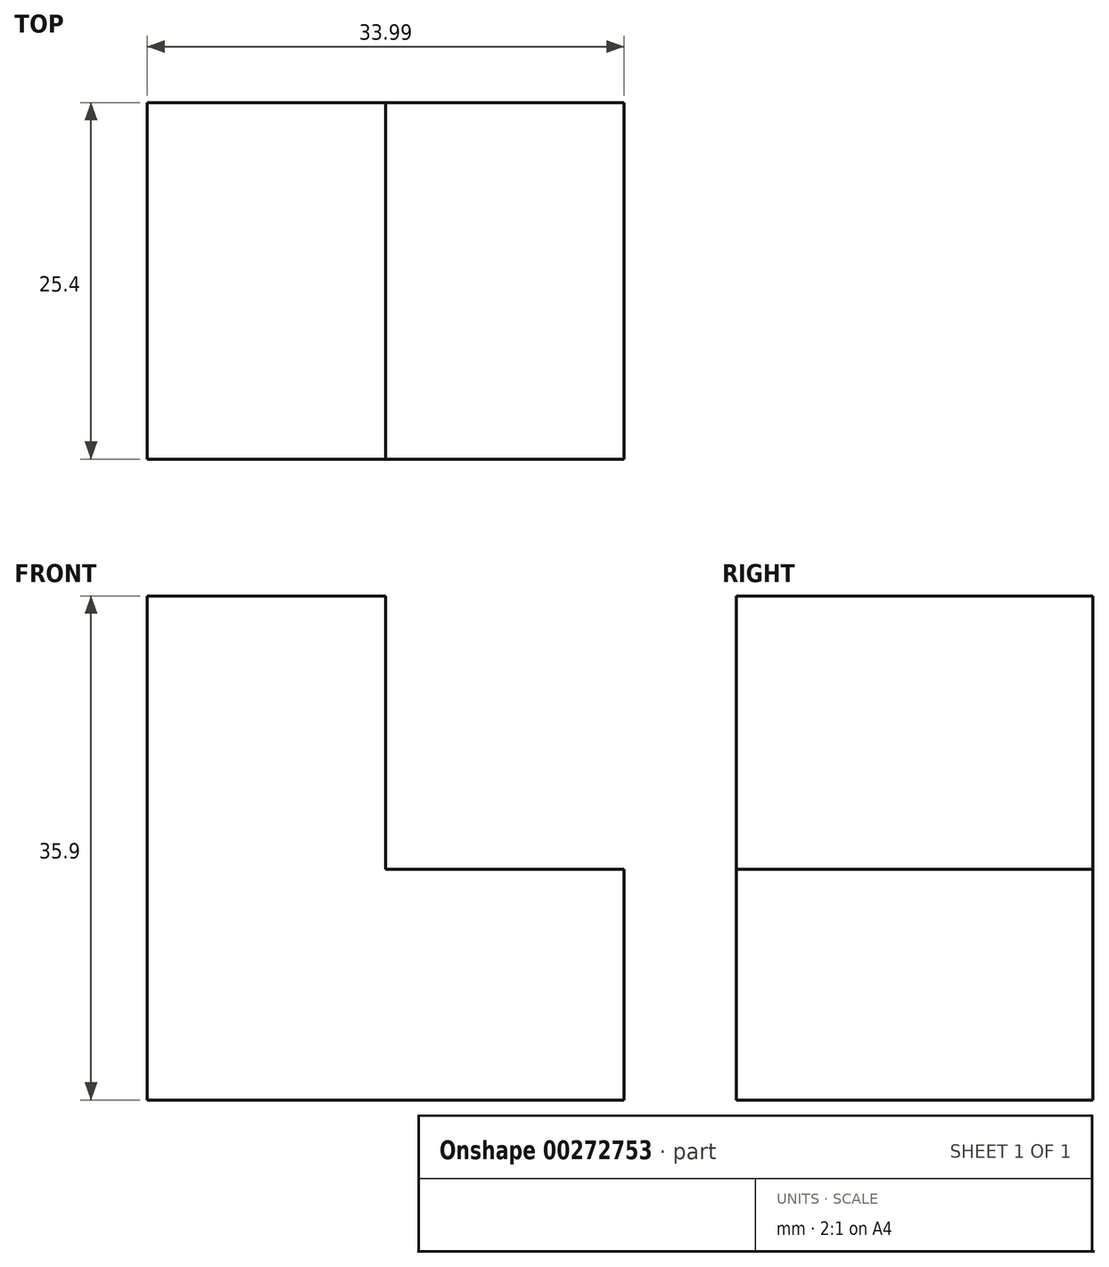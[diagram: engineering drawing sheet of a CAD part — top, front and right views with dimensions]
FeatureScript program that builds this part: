
annotation { "Feature Type Name" : "Feature", "Feature Type Description" : "" }
export const myFeature = defineFeature(function(context is Context, id is Id, definition is map)
    precondition{}
    {
        {
            var Q0;
            Q0=qCreatedBy(makeId("Front.planeOp"),FACE);
            var sketch = newSketch(context, id + "F0", { "sketchPlane" : qUnion([Q0])});
            skLineSegment(sketch, "E0", {"start": v(-60.91, 35.9) * mm, "end": v(-60.91, 0) * mm});
            skLineSegment(sketch, "E1", {"start": v(-60.91, 0) * mm, "end": v(-34.18, 0) * mm});
            skLineSegment(sketch, "E2", {"start": v(-60.91, 35.9) * mm, "end": v(-43.92, 35.9) * mm});
            skLineSegment(sketch, "E3", {"start": v(-43.92, 35.9) * mm, "end": v(-43.92, 16.42) * mm});
            skLineSegment(sketch, "E4", {"start": v(-43.92, 16.42) * mm, "end": v(-26.92, 16.42) * mm});
            skLineSegment(sketch, "E5", {"start": v(-26.92, 16.42) * mm, "end": v(-26.92, 0) * mm});
            skLineSegment(sketch, "E6", {"start": v(-26.92, 0) * mm, "end": v(-34.18, 0) * mm});
            skSolve(sketch);
        }
        {
            var Q0;
            Q0=makeQuery(id+"F0.imprint","IMPRINT",FACE,{"disambiguationData":[TD([[makeQuery(id+"F0.imprint","IMPRINT",EDGE,{"derivedFrom":sQuery(id+"F0.wireOp",EDGE,"E0")}),1.0]])]});
            extrude(context, id + "F1", {"entities" : qUnion([Q0]), "depth" : 25.4 * mm});
        }
    });
